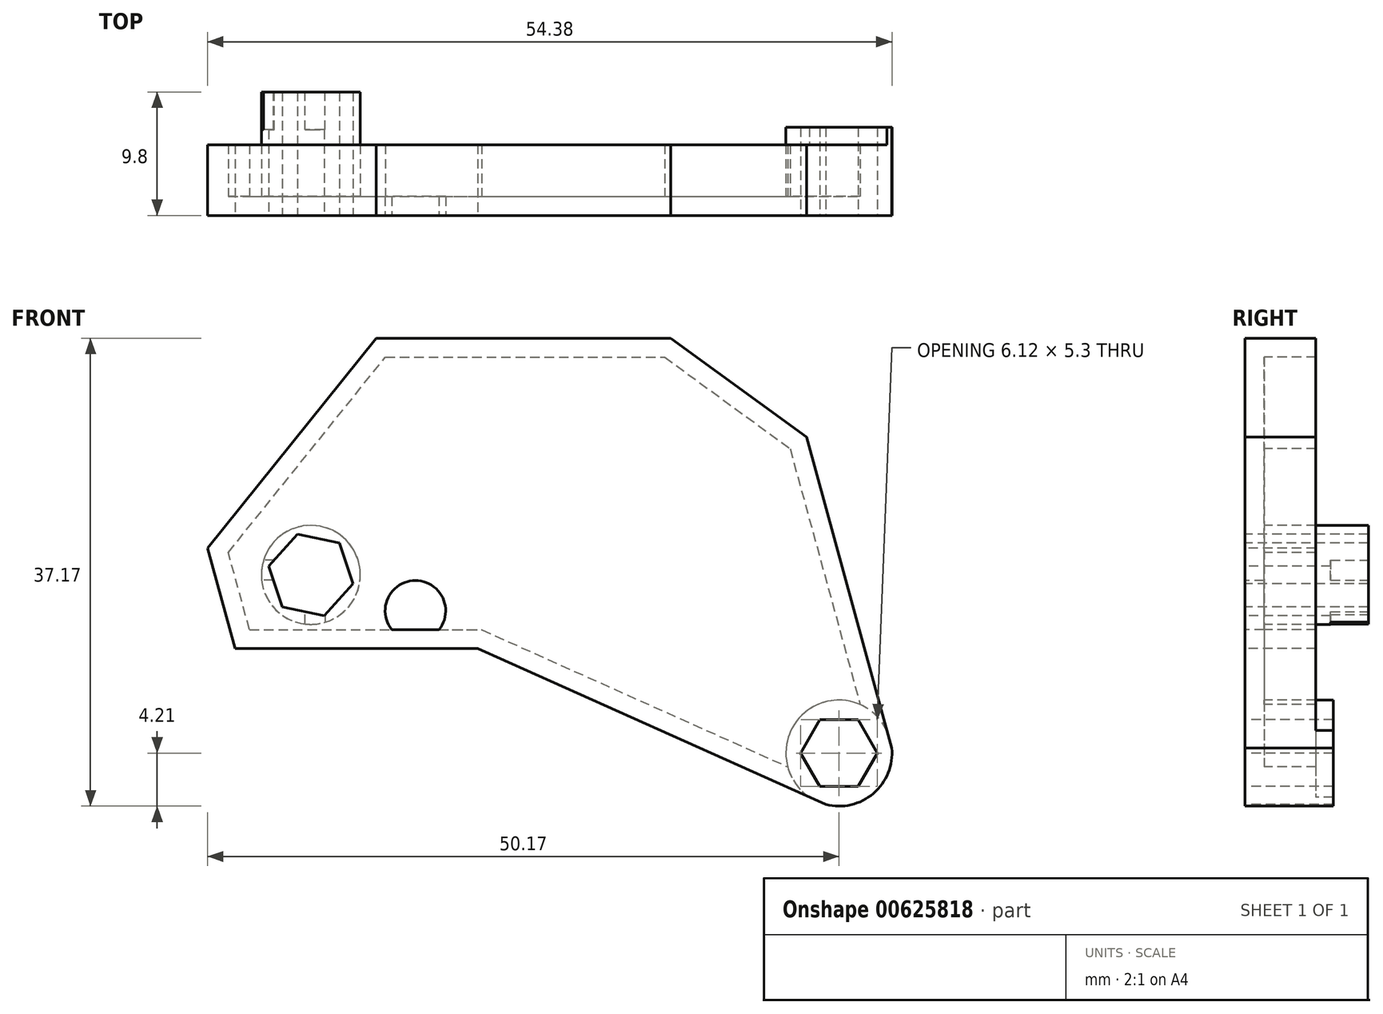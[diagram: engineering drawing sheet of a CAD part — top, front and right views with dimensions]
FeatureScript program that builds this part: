
annotation { "Feature Type Name" : "Feature", "Feature Type Description" : "" }
export const myFeature = defineFeature(function(context is Context, id is Id, definition is map)
    precondition{}
    {
        {
            var Q0;
            Q0=qCreatedBy(makeId("Front.planeOp"),FACE);
            var sketch = newSketch(context, id + "F0", { "sketchPlane" : qUnion([Q0])});
            skCircle(sketch, "E0.0", {"center": v(-9.33, -0.59) * mm, "radius": 1.5 * mm});
            skCircle(sketch, "E1.0", {"center": v(-17.64, 2.27) * mm, "radius": 1.13 * mm});
            skPoint(sketch, "E2.0", {"position": v(-24.62, 17.95) * mm});
            skCircle(sketch, "E3", {"center": v(-17.64, 2.27) * mm, "radius": 3.93 * mm});
            skCircle(sketch, "E4.cCircle", {"center": v(-17.64, 2.27) * mm, "radius": 2.95 * mm, "construction": true});
            skLineSegment(sketch, "E4.0", {"start": v(-19.9, -0.27) * mm, "end": v(-20.97, 2.97) * mm});
            skLineSegment(sketch, "E4.1", {"start": v(-20.97, 2.97) * mm, "end": v(-18.7, 5.5) * mm});
            skLineSegment(sketch, "E4.2", {"start": v(-18.7, 5.5) * mm, "end": v(-15.37, 4.81) * mm});
            skLineSegment(sketch, "E4.3", {"start": v(-15.37, 4.81) * mm, "end": v(-14.3, 1.58) * mm});
            skLineSegment(sketch, "E4.4", {"start": v(-14.3, 1.58) * mm, "end": v(-16.57, -0.97) * mm});
            skLineSegment(sketch, "E4.5", {"start": v(-16.57, -0.97) * mm, "end": v(-19.9, -0.27) * mm});
            skCircle(sketch, "E5", {"center": v(-17.64, 2.27) * mm, "radius": 1.5 * mm});
            skLineSegment(sketch, "E6", {"start": v(-22.5, -2.09) * mm, "end": v(-4.06, -2.09) * mm});
            skLineSegment(sketch, "E7", {"start": v(-22.5, -2.09) * mm, "end": v(-24.2, 4.04) * mm});
            skLineSegment(sketch, "E8", {"start": v(-24.2, 4.04) * mm, "end": v(-11.71, 19.57) * mm});
            skLineSegment(sketch, "E9", {"start": v(-11.71, 19.57) * mm, "end": v(10.47, 19.57) * mm});
            skLineSegment(sketch, "E10", {"start": v(10.47, 19.57) * mm, "end": v(20.43, 12.3) * mm});
            skLineSegment(sketch, "E11", {"start": v(20.43, 12.3) * mm, "end": v(26.88, -11.19) * mm});
            skLineSegment(sketch, "E12", {"start": v(-4.06, -2.09) * mm, "end": v(23.24, -14.3) * mm});
            skLineSegment(sketch, "E13.0", {"start": v(21.74, 13.2) * mm, "end": v(28.51, -11.49) * mm});
            skLineSegment(sketch, "E13.1", {"start": v(10.96, 21.07) * mm, "end": v(21.74, 13.2) * mm});
            skLineSegment(sketch, "E13.2", {"start": v(-12.43, 21.07) * mm, "end": v(10.96, 21.07) * mm});
            skLineSegment(sketch, "E13.3", {"start": v(-4.38, -3.59) * mm, "end": v(23.28, -15.97) * mm});
            skLineSegment(sketch, "E13.4", {"start": v(-23.65, -3.59) * mm, "end": v(-4.38, -3.59) * mm});
            skLineSegment(sketch, "E13.5", {"start": v(-23.65, -3.59) * mm, "end": v(-25.85, 4.39) * mm});
            skLineSegment(sketch, "E13.6", {"start": v(-25.85, 4.39) * mm, "end": v(-12.43, 21.07) * mm});
            skCircle(sketch, "E14.0", {"center": v(24.32, -11.9) * mm, "radius": 2.65 * mm});
            skCircle(sketch, "E15.cCircle", {"center": v(24.32, -11.9) * mm, "radius": 2.65 * mm, "construction": true});
            skLineSegment(sketch, "E15.0", {"start": v(22.79, -9.24) * mm, "end": v(25.85, -9.24) * mm});
            skLineSegment(sketch, "E15.1", {"start": v(25.85, -9.24) * mm, "end": v(27.38, -11.9) * mm});
            skLineSegment(sketch, "E15.2", {"start": v(27.38, -11.9) * mm, "end": v(25.85, -14.54) * mm});
            skLineSegment(sketch, "E15.3", {"start": v(25.85, -14.54) * mm, "end": v(22.79, -14.54) * mm});
            skLineSegment(sketch, "E15.4", {"start": v(22.79, -14.54) * mm, "end": v(21.26, -11.9) * mm});
            skLineSegment(sketch, "E15.5", {"start": v(21.26, -11.9) * mm, "end": v(22.79, -9.24) * mm});
            skPoint(sketch, "E15.0.midPoint", {"position": v(24.32, -9.24) * mm});
            skCircle(sketch, "E16", {"center": v(24.32, -11.9) * mm, "radius": 4.21 * mm});
            skArc(sketch, "E17", {"start": v(-7.45, -2.09) * mm, "mid": v(-9.33, 1.81) * mm, "end": v(-11.2, -2.09) * mm});
            skSolve(sketch);
        }
        {
            var Q0;
            Q0=makeQuery(id+"F0.imprint","IMPRINT",FACE,{"disambiguationData":[TD([[makeQuery(id+"F0.imprint","IMPRINT",EDGE,{"derivedFrom":sQuery(id+"F0.wireOp",EDGE,"E3")}),-1.0]])]});
            extrude(context, id + "F1", {"entities" : qUnion([Q0]), "oppositeDirection" : true, "depth" : 1.5 * mm, "offsetDistance" : 25 * mm});
        }
        {
            var Q0;
            {var subQ8=sQuery(id+"F0.wireOp",EDGE,"E7");Q0=makeQuery(id+"F0.imprint","IMPRINT",FACE,{"disambiguationData":[TD([[makeQuery(id+"F0.imprint","IMPRINT",EDGE,{"derivedFrom":subQ8}),1.0]])]});}
            var Q1;
            {var subQ0=sQuery(id+"F0.wireOp",EDGE,"E6");var subQ1=makeQuery(id+"F0.imprint","INTERSECT",VERTEX,{"derivedFrom":[sQuery(id+"F0.wireOp",EDGE,"E0.0"),subQ0]});Q1=makeQuery(id+"F0.imprint","IMPRINT",FACE,{"disambiguationData":[TD([[makeQuery(id+"F0.imprint","IMPRINT",EDGE,{"disambiguationData":[TD([[subQ1,1.0]])],"derivedFrom":subQ0}),-1.0]])]});}
            extrude(context, id + "F2", {"entities" : qUnion([Q0, Q1]), "operationType" : NewBodyOperationType.ADD, "oppositeDirection" : true, "depth" : 5.62 * mm, "offsetDistance" : 25 * mm});
        }
        {
            var Q0;
            Q0=makeQuery(id+"F0.imprint","IMPRINT",FACE,{"disambiguationData":[TD([[makeQuery(id+"F0.imprint","IMPRINT",EDGE,{"derivedFrom":sQuery(id+"F0.wireOp",EDGE,"E3")}),1.0]])]});
            extrude(context, id + "F3", {"entities" : qUnion([Q0]), "operationType" : NewBodyOperationType.ADD, "oppositeDirection" : true, "depth" : 9.8 * mm, "offsetDistance" : 25 * mm});
        }
        {
            var Q0;
            {var subQ9=sQuery(id+"F0.wireOp",EDGE,"E16");var subQ16=sQuery(id+"F0.wireOp",EDGE,"E11");var subQ19=makeQuery(id+"F0.imprint","INTERSECT",VERTEX,{"derivedFrom":[subQ16,subQ9]});Q0=makeQuery(id+"F0.imprint","IMPRINT",FACE,{"disambiguationData":[TD([[makeQuery(id+"F0.imprint","IMPRINT",EDGE,{"disambiguationData":[TD([[subQ19,-1.0]])],"derivedFrom":subQ16}),1.0]])]});}
            var Q1;
            {var subQ12=sQuery(id+"F0.wireOp",EDGE,"E11");var subQ14=sQuery(id+"F0.wireOp",EDGE,"E16");var subQ18=makeQuery(id+"F0.imprint","INTERSECT",VERTEX,{"derivedFrom":[subQ12,subQ14]});Q1=makeQuery(id+"F0.imprint","IMPRINT",FACE,{"disambiguationData":[TD([[makeQuery(id+"F0.imprint","IMPRINT",EDGE,{"disambiguationData":[TD([[subQ18,-1.0]])],"derivedFrom":subQ12}),-1.0]])]});}
            extrude(context, id + "F4", {"entities" : qUnion([Q0, Q1]), "operationType" : NewBodyOperationType.ADD, "oppositeDirection" : true, "depth" : 7 * mm, "offsetDistance" : 25 * mm});
        }
        {
            var Q0;
            Q0=makeQuery(id+"F0.imprint","IMPRINT",FACE,{"disambiguationData":[TD([[makeQuery(id+"F0.imprint","IMPRINT",EDGE,{"derivedFrom":sQuery(id+"F0.wireOp",EDGE,"E3")}),1.0]])]});
            var sketch = newSketch(context, id + "F5", { "sketchPlane" : qUnion([Q0])});
            skLineSegment(sketch, "E18", {"start": v(-16.28, 0.94) * mm, "end": v(-16.28, -2.5) * mm});
            skLineSegment(sketch, "E19", {"start": v(-16.28, -2.5) * mm, "end": v(-17.78, -2.5) * mm});
            skLineSegment(sketch, "E20", {"start": v(-17.78, -2.5) * mm, "end": v(-17.78, 1.23) * mm});
            skLineSegment(sketch, "E21", {"start": v(-17.78, 1.23) * mm, "end": v(-16.28, 0.94) * mm});
            skLineSegment(sketch, "E22.bottom", {"start": v(-21.75, 3.54) * mm, "end": v(-18.68, 3.54) * mm});
            skLineSegment(sketch, "E22.top", {"start": v(-21.75, 2.04) * mm, "end": v(-18.68, 2.04) * mm});
            skLineSegment(sketch, "E22.left", {"start": v(-21.75, 3.54) * mm, "end": v(-21.75, 2.04) * mm});
            skLineSegment(sketch, "E22.right", {"start": v(-18.68, 3.54) * mm, "end": v(-18.68, 2.04) * mm});
            skSolve(sketch);
        }
        {
            var Q0;
            Q0=makeQuery(id+"F3.opExtrude","CAP_FACE",FACE,{"disambiguationData":[OSD([sQuery(id+"F0.wireOp",EDGE,"E3"),sQuery(id+"F0.wireOp",EDGE,"E4.0"),sQuery(id+"F0.wireOp",EDGE,"E4.1"),sQuery(id+"F0.wireOp",EDGE,"E4.2"),sQuery(id+"F0.wireOp",EDGE,"E4.3"),sQuery(id+"F0.wireOp",EDGE,"E4.4"),sQuery(id+"F0.wireOp",EDGE,"E4.5")])],"isStart":false});
            var sketch = newSketch(context, id + "F6", { "sketchPlane" : qUnion([Q0])});
            skPoint(sketch, "E23.0", {"position": v(18.68, 1.85) * mm});
            skPoint(sketch, "E24.0", {"position": v(17.78, 1.23) * mm});
            skPoint(sketch, "E25.0", {"position": v(16.28, 0.94) * mm});
            skPoint(sketch, "E26.0", {"position": v(16.28, -2.5) * mm});
            skPoint(sketch, "E27.0", {"position": v(17.78, -2.5) * mm});
            skLineSegment(sketch, "E28.bottom", {"start": v(18.68, 1.85) * mm, "end": v(21.77, 1.85) * mm});
            skLineSegment(sketch, "E28.top", {"start": v(18.68, 3.45) * mm, "end": v(21.77, 3.45) * mm});
            skLineSegment(sketch, "E28.left", {"start": v(18.68, 1.85) * mm, "end": v(18.68, 3.45) * mm});
            skLineSegment(sketch, "E28.right", {"start": v(21.77, 1.85) * mm, "end": v(21.77, 3.45) * mm});
            skLineSegment(sketch, "E29", {"start": v(16.5, 1.07) * mm, "end": v(16.5, -1.86) * mm});
            skLineSegment(sketch, "E30", {"start": v(16.5, -1.86) * mm, "end": v(18.1, -1.86) * mm});
            skLineSegment(sketch, "E31", {"start": v(18.1, -1.86) * mm, "end": v(18.1, 1.37) * mm});
            skLineSegment(sketch, "E32", {"start": v(16.5, 1.07) * mm, "end": v(18.1, 1.37) * mm});
            skSolve(sketch);
        }
        {
            var Q0;
            {var subQ0=sQuery(id+"F6.wireOp",EDGE,"E29");var subQ1=makeQuery(id+"F3.opExtrude","CAP_EDGE",EDGE,{"disambiguationData":[OSD([sQuery(id+"F0.wireOp",EDGE,"E3")])],"isStart":false});var subQ2=makeQuery(id+"F6.imprint","INTERSECT",VERTEX,{"derivedFrom":[subQ1,subQ0]});Q0=makeQuery(id+"F6.imprint","IMPRINT",FACE,{"disambiguationData":[TD([[makeQuery(id+"F6.imprint","IMPRINT",EDGE,{"disambiguationData":[TD([[subQ2,1.0]])],"derivedFrom":subQ0}),1.0]])]});}
            var Q1;
            {var subQ3=sQuery(id+"F6.wireOp",EDGE,"E28.bottom");var subQ6=makeQuery(id+"F3.opExtrude","CAP_EDGE",EDGE,{"disambiguationData":[OSD([sQuery(id+"F0.wireOp",EDGE,"E3")])],"isStart":false});var subQ9=makeQuery(id+"F6.imprint","INTERSECT",VERTEX,{"derivedFrom":[subQ6,subQ3]});Q1=makeQuery(id+"F6.imprint","IMPRINT",FACE,{"disambiguationData":[TD([[makeQuery(id+"F6.imprint","IMPRINT",EDGE,{"disambiguationData":[TD([[subQ9,1.0]])],"derivedFrom":subQ3}),1.0]])]});}
            extrude(context, id + "F7", {"entities" : qUnion([Q0, Q1]), "operationType" : NewBodyOperationType.REMOVE, "oppositeDirection" : true, "depth" : 3 * mm, "offsetDistance" : 25 * mm});
        }
    });
